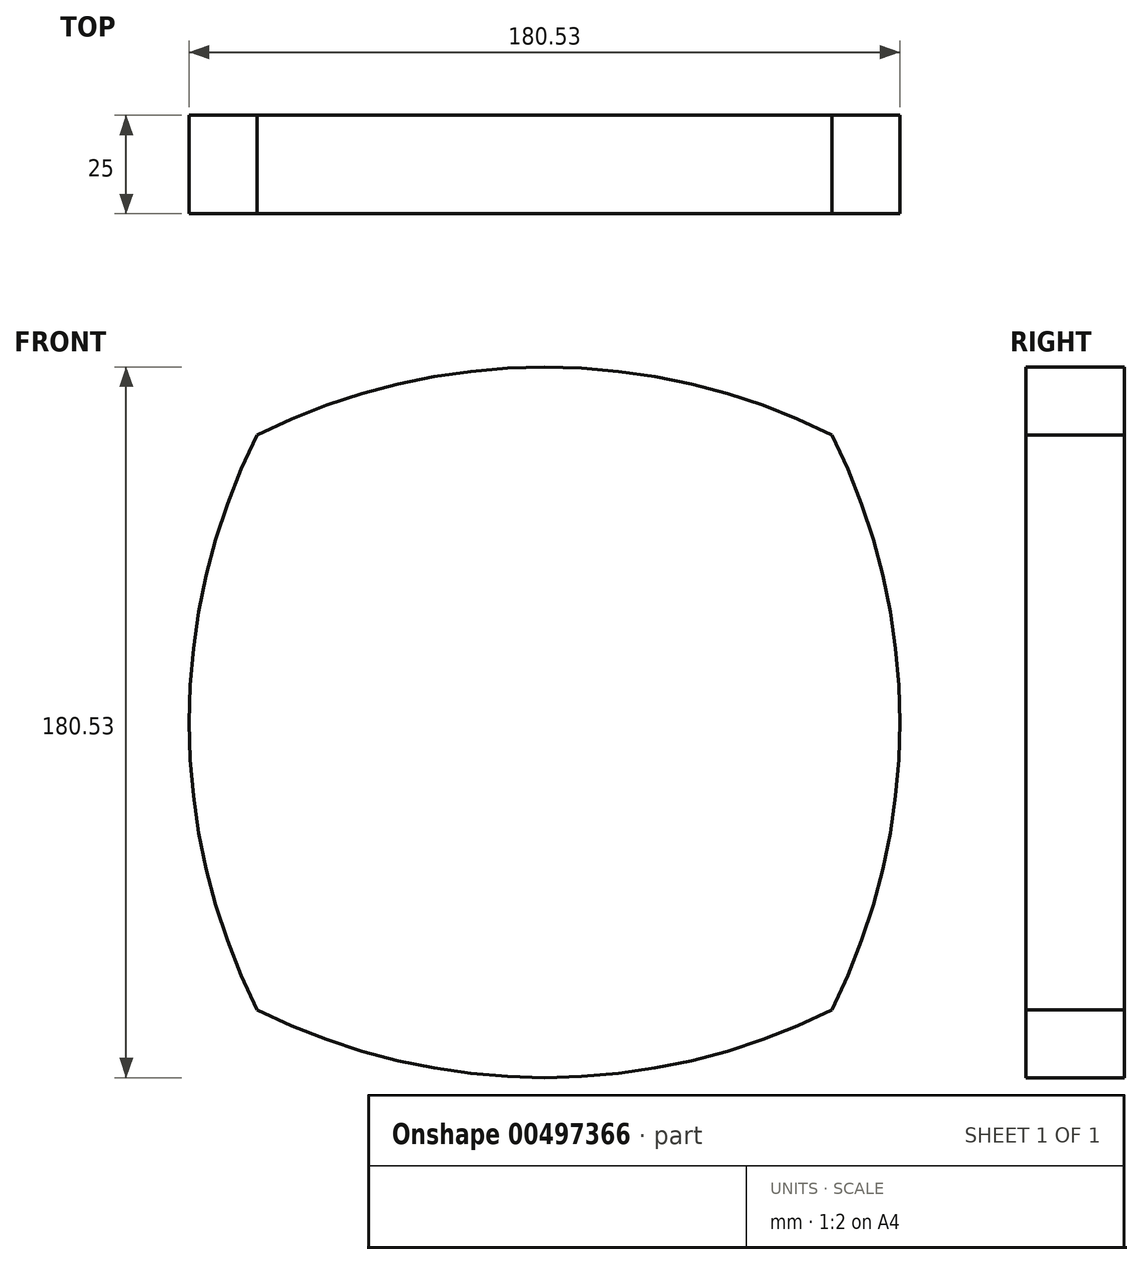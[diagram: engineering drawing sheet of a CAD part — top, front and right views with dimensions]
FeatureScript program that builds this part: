
annotation { "Feature Type Name" : "Feature", "Feature Type Description" : "" }
export const myFeature = defineFeature(function(context is Context, id is Id, definition is map)
    precondition{}
    {
        {
            var Q0;
            Q0=qCreatedBy(makeId("Front.planeOp"),FACE);
            var sketch = newSketch(context, id + "F0", { "sketchPlane" : qUnion([Q0])});
            skArc(sketch, "E0", {"start": v(0, 0) * mm, "mid": v(73.03, 17.24) * mm, "end": v(146.05, 0) * mm});
            skArc(sketch, "E1", {"start": v(0, 0) * mm, "mid": v(-17.24, -73.03) * mm, "end": v(0, -146.05) * mm});
            skArc(sketch, "E2", {"start": v(146.05, 0) * mm, "mid": v(163.29, -73.03) * mm, "end": v(146.05, -146.05) * mm});
            skArc(sketch, "E3", {"start": v(0, -146.05) * mm, "mid": v(73.03, -163.29) * mm, "end": v(146.05, -146.05) * mm});
            skArc(sketch, "E4", {"start": v(81.78, -297.35) * mm, "mid": v(129.4, -286.1) * mm, "end": v(177.03, -297.35) * mm});
            skArc(sketch, "E5", {"start": v(177.03, -297.35) * mm, "mid": v(188.27, -344.97) * mm, "end": v(177.03, -392.6) * mm});
            skArc(sketch, "E6", {"start": v(81.78, -297.35) * mm, "mid": v(70.53, -344.97) * mm, "end": v(81.78, -392.6) * mm});
            skArc(sketch, "E7", {"start": v(81.78, -392.6) * mm, "mid": v(129.4, -403.84) * mm, "end": v(177.03, -392.6) * mm});
            skSolve(sketch);
        }
        {
            var Q0;
            Q0=sQuery(id+"F0.wireOp",EDGE,"E2");
            var Q1;
            Q1=sQuery(id+"F0.wireOp",EDGE,"E0");
            var Q2;
            Q2=sQuery(id+"F0.wireOp",EDGE,"E1");
            var Q3;
            Q3=sQuery(id+"F0.wireOp",EDGE,"E3");
            extrude(context, id + "F1", {"bodyType" : ToolBodyType.SURFACE, "surfaceEntities" : qUnion([Q0, Q1, Q2, Q3]), "depth" : 25 * mm});
        }
    });
